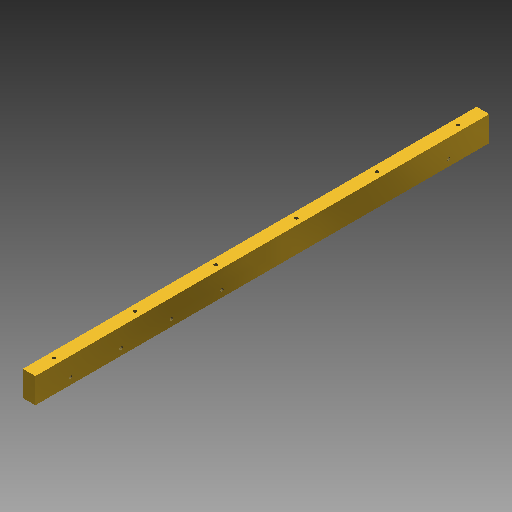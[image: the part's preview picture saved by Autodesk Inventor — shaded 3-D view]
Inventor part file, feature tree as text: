
AUTODESK INVENTOR PART (.ipt)
format: ipt  version: 2017 (Build 210142000, 142)  size: 124,416 bytes
history: native  units: in
note: dims shown in document units (in); Inventor stores cm internally (conversion verified against a paired STEP export)
features: sketch x3, hole x3, pattern_linear x2, extrude x1
ambient origin geometry x8: Origin, YZ Plane, XZ Plane, XY Plane, X Axis, Y Axis, Z Axis, Center Point
bodies: Solid1 (feature_tree)
feature tree (9):
  extrude  "Extrusion1"  Depth=0.5in
  sketch  "Sketch3"  dims[d6=9.0in d7=0.0in d8=0.3703in]
  hole  "Hole1"  [1 undecoded]
  pattern_linear  "Rectangular Pattern1"  Count1=4 Spacing1=1.0in
  hole  "Hole5"  [1 undecoded]
  hole  "Hole6"  [1 undecoded]
  pattern_linear  "Rectangular Pattern5"  Spacing1=0.5in  [1 undecoded]
  sketch  "Sketch2"  dims[d3=0.25in d5=0.5in]
  sketch  "Sketch7"  dims[d9=0.7in d10=0.067in d11=0.75in d12=0.375in d13=0.25in d14=0.5635in d15=1.0in d16=0.8108in d17=1.5748in d19=1.0in d60=8.2in d61=0.3703in d62=0.067in d63=0.75in d64=0.375in d65=0.25in d66=0.5635in d67=1.0in d68=0.8108in d69=0.5in d70=0.125in d71=0.067in d72=0.75in d73=0.375in d74=0.25in d75=0.5635in d76=0.25in d77=0.8108in d78=2.3622in d80=1.6in]
note: 4 required parameter values undecoded (feature->parameter linkage not recoverable at this tier; creation-order binding heuristic only, values carry confidence <= 0.55)
